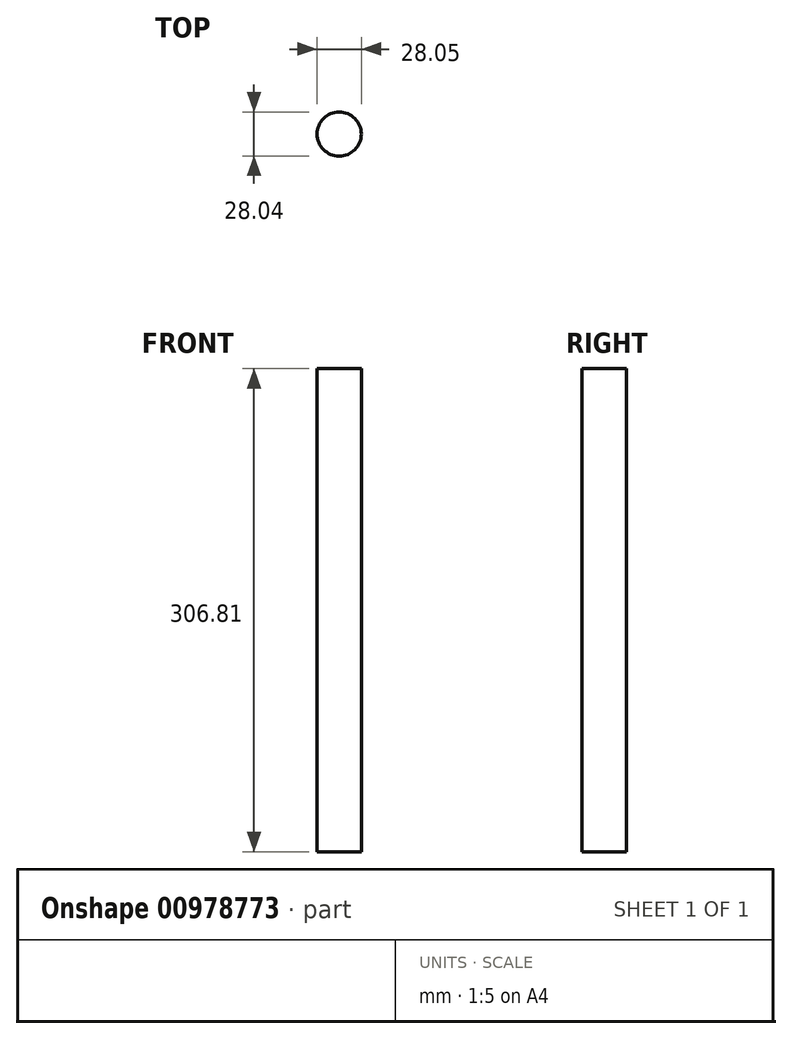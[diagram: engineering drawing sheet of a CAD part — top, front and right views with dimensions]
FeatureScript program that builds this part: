
annotation { "Feature Type Name" : "Feature", "Feature Type Description" : "" }
export const myFeature = defineFeature(function(context is Context, id is Id, definition is map)
    precondition{}
    {
        {
            var Q0;
            Q0=qCreatedBy(makeId("Top.planeOp"),FACE);
            var sketch = newSketch(context, id + "F0", { "sketchPlane" : qUnion([Q0])});
            skCircle(sketch, "E0", {"center": v(47.8, 0) * mm, "radius": 14.02 * mm});
            skSolve(sketch);
        }
        {
            var Q0;
            Q0=makeQuery(id+"F0.imprint","IMPRINT",FACE,{"disambiguationData":[TD([[makeQuery(id+"F0.imprint","IMPRINT",EDGE,{"derivedFrom":sQuery(id+"F0.wireOp",EDGE,"E0")}),1.0]])]});
            extrude(context, id + "F1", {"entities" : qUnion([Q0]), "depth" : 306.8 * mm, "offsetDistance" : 25.4 * mm});
        }
    });
